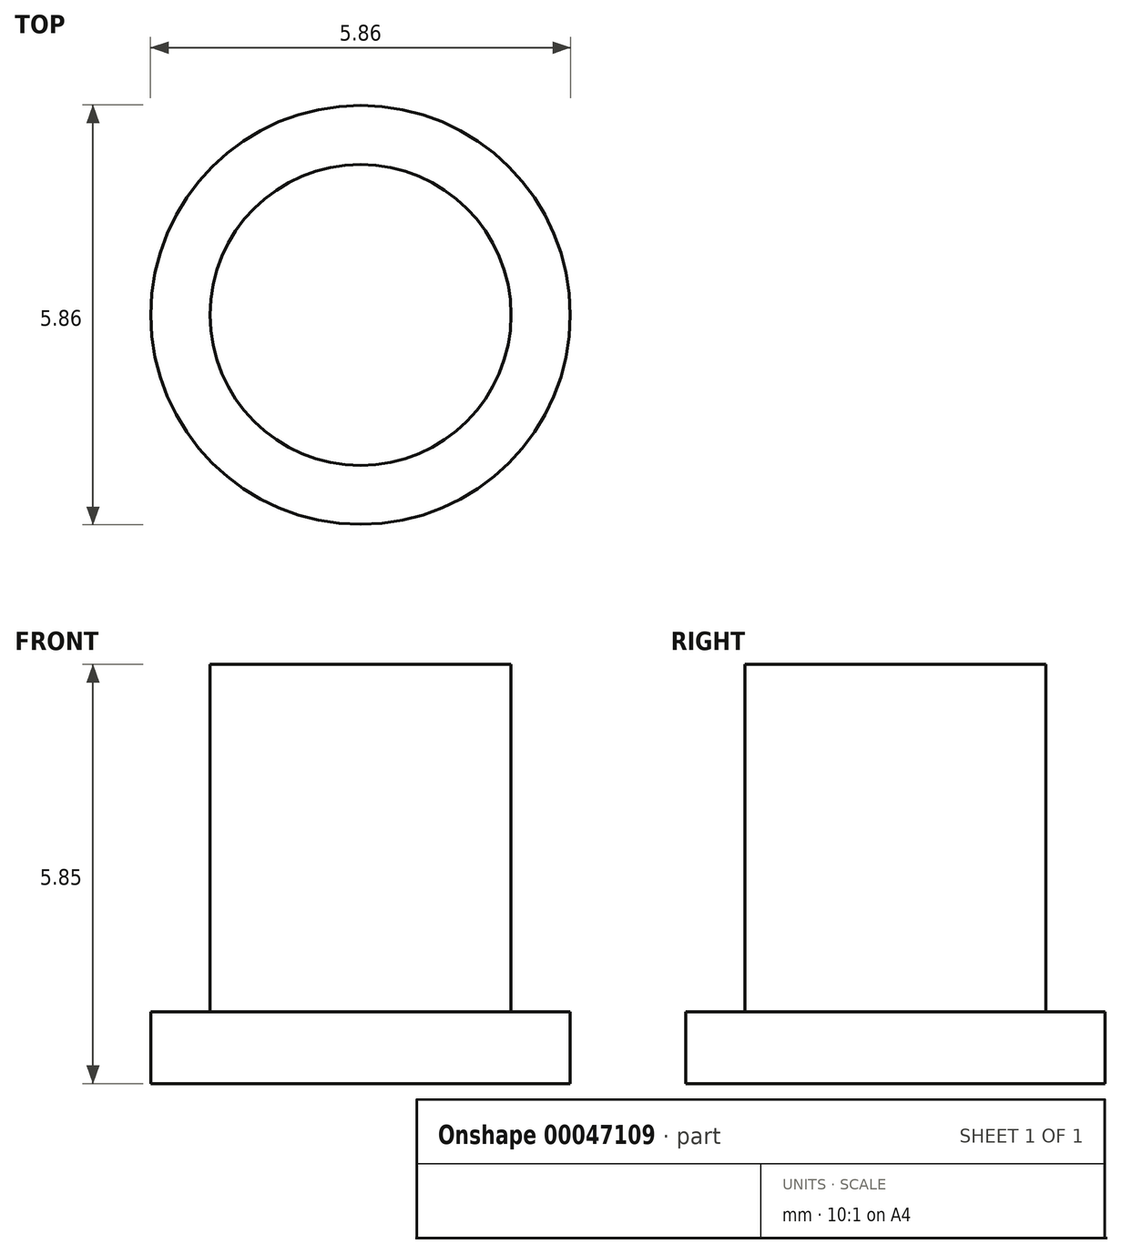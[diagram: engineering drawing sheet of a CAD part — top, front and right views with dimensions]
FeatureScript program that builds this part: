
annotation { "Feature Type Name" : "Feature", "Feature Type Description" : "" }
export const myFeature = defineFeature(function(context is Context, id is Id, definition is map)
    precondition{}
    {
        {
            assignVariable(context, id + "F0", {"name" : "dia_out", "anyValue" : 5.85});
        }
        {
            assignVariable(context, id + "F1", {"name" : "extrude_disk", "anyValue" : 1});
        }
        {
            var Q0;
            Q0=qCreatedBy(makeId("Top.planeOp"),FACE);
            var sketch = newSketch(context, id + "F2", { "sketchPlane" : qUnion([Q0])});
            skCircle(sketch, "E0", {"center": v(0, 0) * mm, "radius": 2.93 * mm});
            skCircle(sketch, "E1", {"center": v(0, 0) * mm, "radius": 2.1 * mm});
            skSolve(sketch);
        }
        {
            var Q0;
            Q0=makeQuery(id+"F2.imprint","IMPRINT",FACE,{"disambiguationData":[TD([[makeQuery(id+"F2.imprint","IMPRINT",EDGE,{"derivedFrom":sQuery(id+"F2.wireOp",EDGE,"E0")}),1.0]])]});
            var Q1;
            Q1=makeQuery(id+"F2.imprint","IMPRINT",FACE,{"disambiguationData":[TD([[makeQuery(id+"F2.imprint","IMPRINT",EDGE,{"derivedFrom":sQuery(id+"F2.wireOp",EDGE,"E1")}),1.0]])]});
            extrude(context, id + "F3", {"entities" : qUnion([Q0, Q1]), "depth" : (getVariable(context, 'extrude_disk')) * mm});
        }
        {
            var Q0;
            Q0=makeQuery(id+"F2.imprint","IMPRINT",FACE,{"disambiguationData":[TD([[makeQuery(id+"F2.imprint","IMPRINT",EDGE,{"derivedFrom":sQuery(id+"F2.wireOp",EDGE,"E1")}),1.0]])]});
            extrude(context, id + "F4", {"entities" : qUnion([Q0]), "operationType" : NewBodyOperationType.ADD, "depth" : (getVariable(context, 'dia_out')) * mm});
        }
    });
